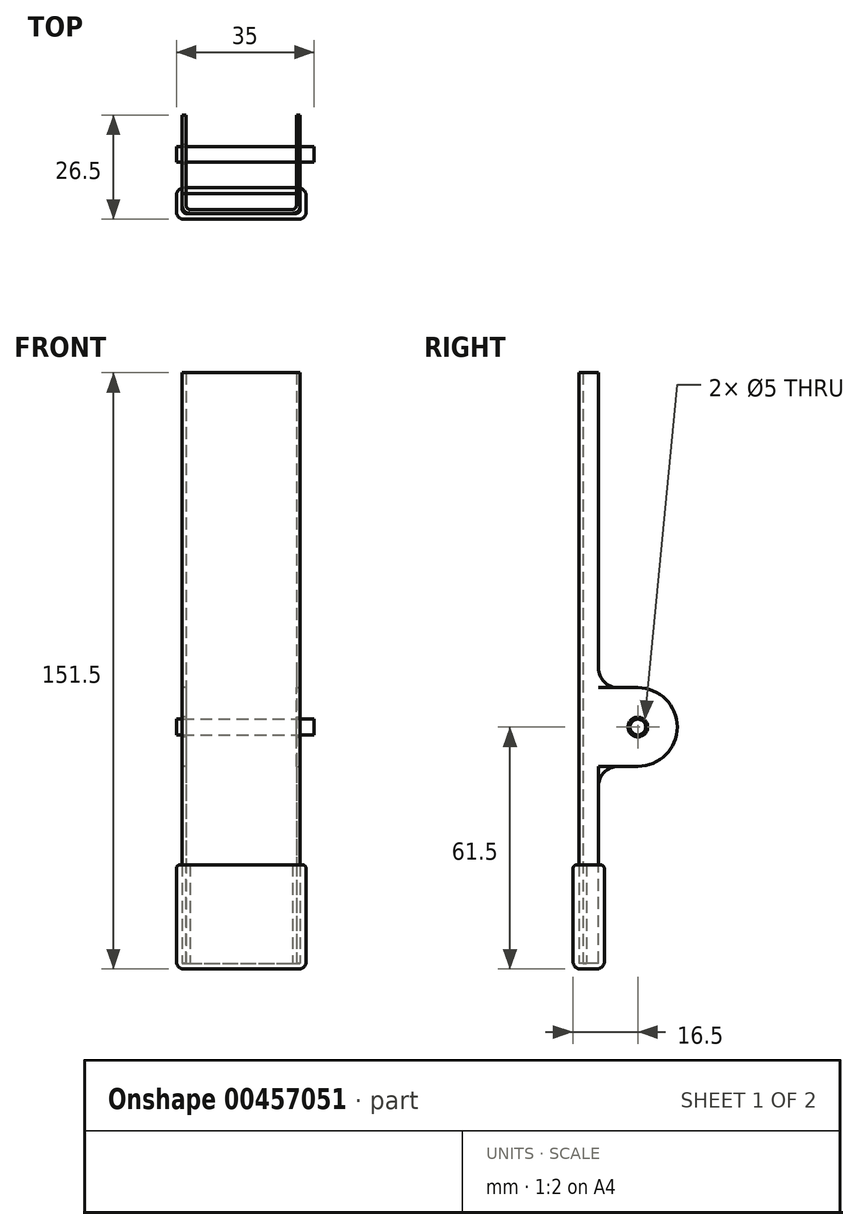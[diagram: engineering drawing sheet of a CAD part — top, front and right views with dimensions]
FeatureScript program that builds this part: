
annotation { "Feature Type Name" : "Feature", "Feature Type Description" : "" }
export const myFeature = defineFeature(function(context is Context, id is Id, definition is map)
    precondition{}
    {
        {
            var Q0;
            Q0=qCreatedBy(makeId("Top.planeOp"),FACE);
            var sketch = newSketch(context, id + "F0", { "sketchPlane" : qUnion([Q0])});
            skLineSegment(sketch, "E0.bottom", {"start": v(2, 0) * mm, "end": v(28, 0) * mm});
            skLineSegment(sketch, "E0.left", {"start": v(0, 2) * mm, "end": v(0, 5) * mm});
            skLineSegment(sketch, "E0.right", {"start": v(30, 2) * mm, "end": v(30, 5) * mm});
            skLineSegment(sketch, "E1.top", {"start": v(2, 1) * mm, "end": v(28, 1) * mm});
            skLineSegment(sketch, "E1.left", {"start": v(1, 5) * mm, "end": v(1, 2) * mm});
            skLineSegment(sketch, "E1.right", {"start": v(29, 5) * mm, "end": v(29, 2) * mm});
            skLineSegment(sketch, "E2", {"start": v(1, 5) * mm, "end": v(0, 5) * mm});
            skLineSegment(sketch, "E3", {"start": v(30, 5) * mm, "end": v(29, 5) * mm});
            skPoint(sketch, "E4.visualSharp", {"position": v(29, 1) * mm});
            skArc(sketch, "E4.filletArc", {"start": v(28, 1) * mm, "mid": v(28.7, 1.3) * mm, "end": v(29, 2) * mm});
            skPoint(sketch, "E5.visualSharp", {"position": v(1, 1) * mm});
            skArc(sketch, "E5.filletArc", {"start": v(1, 2) * mm, "mid": v(1.3, 1.3) * mm, "end": v(2, 1) * mm});
            skPoint(sketch, "E6.visualSharp", {"position": v(0, 0) * mm});
            skArc(sketch, "E6.filletArc", {"start": v(0, 2) * mm, "mid": v(0.59, 0.59) * mm, "end": v(2, 0) * mm});
            skPoint(sketch, "E7.visualSharp", {"position": v(30, 0) * mm});
            skArc(sketch, "E7.filletArc", {"start": v(28, 0) * mm, "mid": v(29.41, 0.59) * mm, "end": v(30, 2) * mm});
            skSolve(sketch);
        }
        {
            var Q0;
            Q0=makeQuery(id+"F0.imprint","IMPRINT",FACE,{"disambiguationData":[TD([[makeQuery(id+"F0.imprint","IMPRINT",EDGE,{"derivedFrom":sQuery(id+"F0.wireOp",EDGE,"E0.bottom")}),1.0]])]});
            extrude(context, id + "F1", {"entities" : qUnion([Q0]), "depth" : 150 * mm});
        }
        {
            var Q0;
            Q0=makeQuery(id+"F1.opExtrude","SWEPT_FACE",FACE,{"disambiguationData":[OSD([sQuery(id+"F0.wireOp",EDGE,"E0.left")])]});
            var sketch = newSketch(context, id + "F2", { "sketchPlane" : qUnion([Q0])});
            skLineSegment(sketch, "E8.bottom", {"start": v(-5, 50) * mm, "end": v(-15, 50) * mm});
            skLineSegment(sketch, "E8.top", {"start": v(-5, 70) * mm, "end": v(-15, 70) * mm});
            skLineSegment(sketch, "E8.left", {"start": v(-5, 50) * mm, "end": v(-5, 70) * mm});
            skLineSegment(sketch, "E8.right", {"start": v(-25, 60) * mm, "end": v(-25, 60) * mm});
            skPoint(sketch, "E9.visualSharp", {"position": v(-25, 50) * mm});
            skArc(sketch, "E9.filletArc", {"start": v(-25, 60) * mm, "mid": v(-22.07, 52.93) * mm, "end": v(-15, 50) * mm});
            skPoint(sketch, "E10.visualSharp", {"position": v(-25, 70) * mm});
            skArc(sketch, "E10.filletArc", {"start": v(-15, 70) * mm, "mid": v(-22.07, 67.07) * mm, "end": v(-25, 60) * mm});
            skCircle(sketch, "E11", {"center": v(-15, 60) * mm, "radius": 2.5 * mm});
            skSolve(sketch);
        }
        {
            var Q0;
            Q0 = qSketchRegion(id + "F2", true);
            extrude(context, id + "F3", {"entities" : qUnion([Q0]), "operationType" : NewBodyOperationType.ADD, "oppositeDirection" : true, "depth" : 1 * mm});
        }
        {
            var Q0;
            Q0=makeQuery(id+"F3.opExtrude","SWEPT_EDGE",EDGE,{"disambiguationData":[OSD([sQuery(id+"F0.wireOp",EDGE,"E0.left"),sQuery(id+"F0.wireOp",EDGE,"E2"),sQuery(id+"F2.wireOp",EDGE,"E8.bottom"),sQuery(id+"F2.wireOp",EDGE,"E8.left")])]});
            var Q1;
            Q1=makeQuery(id+"F3.opExtrude","SWEPT_EDGE",EDGE,{"disambiguationData":[OSD([sQuery(id+"F0.wireOp",EDGE,"E0.left"),sQuery(id+"F0.wireOp",EDGE,"E2"),sQuery(id+"F2.wireOp",EDGE,"E8.top"),sQuery(id+"F2.wireOp",EDGE,"E8.left")])]});
            fillet(context, id + "F4", {"entities" : qUnion([Q0, Q1]), "radius" : 5 * mm, "tangentPropagation" : true, "allowEdgeOverflow" : false});
        }
        {
            var Q0;
            Q0=makeQuery(id+"F1.opExtrude","SWEPT_FACE",FACE,{"disambiguationData":[OSD([sQuery(id+"F0.wireOp",EDGE,"E0.right")])]});
            var sketch = newSketch(context, id + "F5", { "sketchPlane" : qUnion([Q0])});
            skLineSegment(sketch, "E12.bottom", {"start": v(5, 70) * mm, "end": v(15, 70) * mm});
            skLineSegment(sketch, "E12.top", {"start": v(5, 50) * mm, "end": v(15, 50) * mm});
            skLineSegment(sketch, "E12.left", {"start": v(5, 70) * mm, "end": v(5, 50) * mm});
            skLineSegment(sketch, "E12.right", {"start": v(25, 60) * mm, "end": v(25, 60) * mm});
            skPoint(sketch, "E13.visualSharp", {"position": v(25, 70) * mm});
            skArc(sketch, "E13.filletArc", {"start": v(25, 60) * mm, "mid": v(22.07, 67.07) * mm, "end": v(15, 70) * mm});
            skPoint(sketch, "E14.visualSharp", {"position": v(25, 50) * mm});
            skArc(sketch, "E14.filletArc", {"start": v(15, 50) * mm, "mid": v(22.07, 52.93) * mm, "end": v(25, 60) * mm});
            skCircle(sketch, "E15", {"center": v(15, 60) * mm, "radius": 2.5 * mm});
            skSolve(sketch);
        }
        {
            var Q0;
            Q0 = qSketchRegion(id + "F5", true);
            extrude(context, id + "F6", {"entities" : qUnion([Q0]), "operationType" : NewBodyOperationType.ADD, "oppositeDirection" : true, "depth" : 1 * mm});
        }
        {
            var Q0;
            Q0=makeQuery(id+"F6.opExtrude","SWEPT_EDGE",EDGE,{"disambiguationData":[OSD([sQuery(id+"F0.wireOp",EDGE,"E0.right"),sQuery(id+"F0.wireOp",EDGE,"E3"),sQuery(id+"F5.wireOp",EDGE,"E12.bottom"),sQuery(id+"F5.wireOp",EDGE,"E12.left")])]});
            var Q1;
            Q1=makeQuery(id+"F6.opExtrude","SWEPT_EDGE",EDGE,{"disambiguationData":[OSD([sQuery(id+"F0.wireOp",EDGE,"E0.right"),sQuery(id+"F0.wireOp",EDGE,"E3"),sQuery(id+"F5.wireOp",EDGE,"E12.top"),sQuery(id+"F5.wireOp",EDGE,"E12.left")])]});
            fillet(context, id + "F7", {"entities" : qUnion([Q0, Q1]), "radius" : 5 * mm, "tangentPropagation" : true, "allowEdgeOverflow" : false});
        }
        {
            var Q0;
            Q0=makeQuery(id+"F1.opExtrude","SWEPT_BODY",BODY,{"disambiguationData":[OSD([sQuery(id+"F0.wireOp",EDGE,"E0.bottom"),sQuery(id+"F0.wireOp",EDGE,"E0.left"),sQuery(id+"F0.wireOp",EDGE,"E0.right"),sQuery(id+"F0.wireOp",EDGE,"E1.top"),sQuery(id+"F0.wireOp",EDGE,"E1.left"),sQuery(id+"F0.wireOp",EDGE,"E1.right"),sQuery(id+"F0.wireOp",EDGE,"E2"),sQuery(id+"F0.wireOp",EDGE,"E3"),sQuery(id+"F0.wireOp",EDGE,"E4.filletArc"),sQuery(id+"F0.wireOp",EDGE,"E5.filletArc"),sQuery(id+"F0.wireOp",EDGE,"E6.filletArc"),sQuery(id+"F0.wireOp",EDGE,"E7.filletArc")])]});
            transform(context, id + "F8", {"entities" : qUnion([Q0]), "transformType" : TransformType.TRANSLATION_3D, "dx" : 0 * mm, "dy" : 75 * mm, "dz" : 0 * mm, "makeCopy" : true});
        }
        {
            var Q0;
            Q0=makeQuery(id+"F8.opPattern","COPY",BODY,{"derivedFrom":makeQuery(id+"F1.opExtrude","SWEPT_BODY",BODY,{"disambiguationData":[OSD([sQuery(id+"F0.wireOp",EDGE,"E0.bottom"),sQuery(id+"F0.wireOp",EDGE,"E0.left"),sQuery(id+"F0.wireOp",EDGE,"E0.right"),sQuery(id+"F0.wireOp",EDGE,"E1.top"),sQuery(id+"F0.wireOp",EDGE,"E1.left"),sQuery(id+"F0.wireOp",EDGE,"E1.right"),sQuery(id+"F0.wireOp",EDGE,"E2"),sQuery(id+"F0.wireOp",EDGE,"E3"),sQuery(id+"F0.wireOp",EDGE,"E4.filletArc"),sQuery(id+"F0.wireOp",EDGE,"E5.filletArc"),sQuery(id+"F0.wireOp",EDGE,"E6.filletArc"),sQuery(id+"F0.wireOp",EDGE,"E7.filletArc")])]}),"instanceName":"1"});
            deleteBodies(context, id + "F9", {"entities" : qUnion([Q0])});
        }
        {
            var Q0;
            Q0=makeQuery(id+"F6.boolean.opBoolean","MERGE",FACE,{"derivedFrom":[makeQuery(id+"F1.opExtrude","SWEPT_FACE",FACE,{"disambiguationData":[OSD([sQuery(id+"F0.wireOp",EDGE,"E0.right")])]}),makeQuery(id+"F6.opExtrude","CAP_FACE",FACE,{"disambiguationData":[OSD([sQuery(id+"F5.wireOp",EDGE,"E12.bottom"),sQuery(id+"F5.wireOp",EDGE,"E12.top"),sQuery(id+"F5.wireOp",EDGE,"E12.left"),sQuery(id+"F5.wireOp",EDGE,"E13.filletArc"),sQuery(id+"F5.wireOp",EDGE,"E14.filletArc"),sQuery(id+"F5.wireOp",EDGE,"E15")])],"isStart":true})]});
            var sketch = newSketch(context, id + "F10", { "sketchPlane" : qUnion([Q0])});
            skCircle(sketch, "E16", {"center": v(15, 60) * mm, "radius": 2 * mm});
            skSolve(sketch);
        }
        {
            var Q0;
            Q0 = qSketchRegion(id + "F10", true);
            extrude(context, id + "F11", {"entities" : qUnion([Q0]), "oppositeDirection" : true, "depth" : 31.5 * mm, "hasSecondDirection" : true, "secondDirectionOppositeDirection" : false, "secondDirectionDepth" : 3.5 * mm});
        }
        {
            var Q0;
            Q0=makeQuery(id+"F1.opExtrude","CAP_FACE",FACE,{"disambiguationData":[OSD([sQuery(id+"F0.wireOp",EDGE,"E0.bottom"),sQuery(id+"F0.wireOp",EDGE,"E0.left"),sQuery(id+"F0.wireOp",EDGE,"E0.right"),sQuery(id+"F0.wireOp",EDGE,"E1.top"),sQuery(id+"F0.wireOp",EDGE,"E1.left"),sQuery(id+"F0.wireOp",EDGE,"E1.right"),sQuery(id+"F0.wireOp",EDGE,"E2"),sQuery(id+"F0.wireOp",EDGE,"E3"),sQuery(id+"F0.wireOp",EDGE,"E4.filletArc"),sQuery(id+"F0.wireOp",EDGE,"E5.filletArc"),sQuery(id+"F0.wireOp",EDGE,"E6.filletArc"),sQuery(id+"F0.wireOp",EDGE,"E7.filletArc")])],"isStart":true});
            var sketch = newSketch(context, id + "F12", { "sketchPlane" : qUnion([Q0])});
            skLineSegment(sketch, "E17.bottom", {"start": v(1, 0) * mm, "end": v(29, 0) * mm});
            skLineSegment(sketch, "E17.top", {"start": v(0, -5) * mm, "end": v(30, -5) * mm});
            skLineSegment(sketch, "E17.left", {"start": v(0, -1) * mm, "end": v(0, -5) * mm});
            skLineSegment(sketch, "E17.right", {"start": v(30, -1) * mm, "end": v(30, -5) * mm});
            skLineSegment(sketch, "E18.0", {"start": v(31.5, -0.5) * mm, "end": v(31.5, -4.5) * mm});
            skLineSegment(sketch, "E18.1", {"start": v(0.5, 1.5) * mm, "end": v(29.5, 1.5) * mm});
            skLineSegment(sketch, "E18.2", {"start": v(-1.5, -0.5) * mm, "end": v(-1.5, -4.5) * mm});
            skLineSegment(sketch, "E18.3", {"start": v(0.5, -6.5) * mm, "end": v(29.5, -6.5) * mm});
            skPoint(sketch, "E19.visualSharp", {"position": v(-1.5, 1.5) * mm});
            skArc(sketch, "E19.filletArc", {"start": v(0.5, 1.5) * mm, "mid": v(-0.91, 0.91) * mm, "end": v(-1.5, -0.5) * mm});
            skPoint(sketch, "E20.visualSharp", {"position": v(31.5, 1.5) * mm});
            skArc(sketch, "E20.filletArc", {"start": v(31.5, -0.5) * mm, "mid": v(30.91, 0.91) * mm, "end": v(29.5, 1.5) * mm});
            skPoint(sketch, "E21.visualSharp", {"position": v(31.5, -6.5) * mm});
            skArc(sketch, "E21.filletArc", {"start": v(29.5, -6.5) * mm, "mid": v(30.91, -5.91) * mm, "end": v(31.5, -4.5) * mm});
            skPoint(sketch, "E22.visualSharp", {"position": v(-1.5, -6.5) * mm});
            skArc(sketch, "E22.filletArc", {"start": v(-1.5, -4.5) * mm, "mid": v(-0.91, -5.91) * mm, "end": v(0.5, -6.5) * mm});
            skPoint(sketch, "E23.visualSharp", {"position": v(0, 0) * mm});
            skArc(sketch, "E23.filletArc", {"start": v(1, 0) * mm, "mid": v(0.3, -0.3) * mm, "end": v(0, -1) * mm});
            skPoint(sketch, "E24.visualSharp", {"position": v(30, 0) * mm});
            skArc(sketch, "E24.filletArc", {"start": v(30, -1) * mm, "mid": v(29.7, -0.3) * mm, "end": v(29, 0) * mm});
            skSolve(sketch);
        }
        {
            var Q0;
            Q0=makeQuery(id+"F12.imprint","IMPRINT",FACE,{"disambiguationData":[TD([[makeQuery(id+"F12.imprint","IMPRINT",EDGE,{"derivedFrom":sQuery(id+"F12.wireOp",EDGE,"E18.0")}),-1.0]])]});
            extrude(context, id + "F13", {"entities" : qUnion([Q0]), "oppositeDirection" : true, "depth" : 25 * mm});
        }
        {
            var Q0;
            Q0=makeQuery(id+"F13.opExtrude","CAP_FACE",FACE,{"disambiguationData":[OSD([sQuery(id+"F12.wireOp",EDGE,"E17.bottom"),sQuery(id+"F12.wireOp",EDGE,"E17.top"),sQuery(id+"F12.wireOp",EDGE,"E17.left"),sQuery(id+"F12.wireOp",EDGE,"E17.right"),sQuery(id+"F12.wireOp",EDGE,"E18.0"),sQuery(id+"F12.wireOp",EDGE,"E18.1"),sQuery(id+"F12.wireOp",EDGE,"E18.2"),sQuery(id+"F12.wireOp",EDGE,"E18.3"),sQuery(id+"F12.wireOp",EDGE,"E19.filletArc"),sQuery(id+"F12.wireOp",EDGE,"E20.filletArc"),sQuery(id+"F12.wireOp",EDGE,"E21.filletArc"),sQuery(id+"F12.wireOp",EDGE,"E22.filletArc"),sQuery(id+"F12.wireOp",EDGE,"E23.filletArc"),sQuery(id+"F12.wireOp",EDGE,"E24.filletArc")])],"isStart":true});
            var sketch = newSketch(context, id + "F14", { "sketchPlane" : qUnion([Q0])});
            skLineSegment(sketch, "E25.bottom", {"start": v(0.5, 1.5) * mm, "end": v(29.5, 1.5) * mm});
            skLineSegment(sketch, "E25.top", {"start": v(0.5, -6.5) * mm, "end": v(29.5, -6.5) * mm});
            skLineSegment(sketch, "E25.left", {"start": v(-1.5, -0.5) * mm, "end": v(-1.5, -4.5) * mm});
            skLineSegment(sketch, "E25.right", {"start": v(31.5, -0.5) * mm, "end": v(31.5, -4.5) * mm});
            skPoint(sketch, "E26.visualSharp", {"position": v(-1.5, 1.5) * mm});
            skArc(sketch, "E26.filletArc", {"start": v(0.5, 1.5) * mm, "mid": v(-0.91, 0.91) * mm, "end": v(-1.5, -0.5) * mm});
            skPoint(sketch, "E27.visualSharp", {"position": v(-1.5, -6.5) * mm});
            skArc(sketch, "E27.filletArc", {"start": v(-1.5, -4.5) * mm, "mid": v(-0.91, -5.91) * mm, "end": v(0.5, -6.5) * mm});
            skPoint(sketch, "E28.visualSharp", {"position": v(31.5, -6.5) * mm});
            skArc(sketch, "E28.filletArc", {"start": v(29.5, -6.5) * mm, "mid": v(30.91, -5.91) * mm, "end": v(31.5, -4.5) * mm});
            skPoint(sketch, "E29.visualSharp", {"position": v(31.5, 1.5) * mm});
            skArc(sketch, "E29.filletArc", {"start": v(31.5, -0.5) * mm, "mid": v(30.91, 0.91) * mm, "end": v(29.5, 1.5) * mm});
            skSolve(sketch);
        }
        {
            var Q0;
            Q0 = qSketchRegion(id + "F14", true);
            extrude(context, id + "F15", {"entities" : qUnion([Q0]), "operationType" : NewBodyOperationType.ADD, "depth" : 1.5 * mm});
        }
        {
            var Q0;
            Q0=makeQuery(id+"F15.opExtrude","CAP_EDGE",EDGE,{"disambiguationData":[OSD([sQuery(id+"F14.wireOp",EDGE,"E25.bottom")])],"isStart":false});
            fillet(context, id + "F16", {"entities" : qUnion([Q0]), "radius" : 2 * mm, "tangentPropagation" : true, "allowEdgeOverflow" : false});
        }
        {
            var Q0;
            Q0=makeQuery(id+"F13.opExtrude","CAP_EDGE",EDGE,{"disambiguationData":[OSD([sQuery(id+"F12.wireOp",EDGE,"E18.1")])],"isStart":false});
            fillet(context, id + "F17", {"entities" : qUnion([Q0]), "radius" : 1 * mm, "tangentPropagation" : true, "allowEdgeOverflow" : false});
        }
    });
